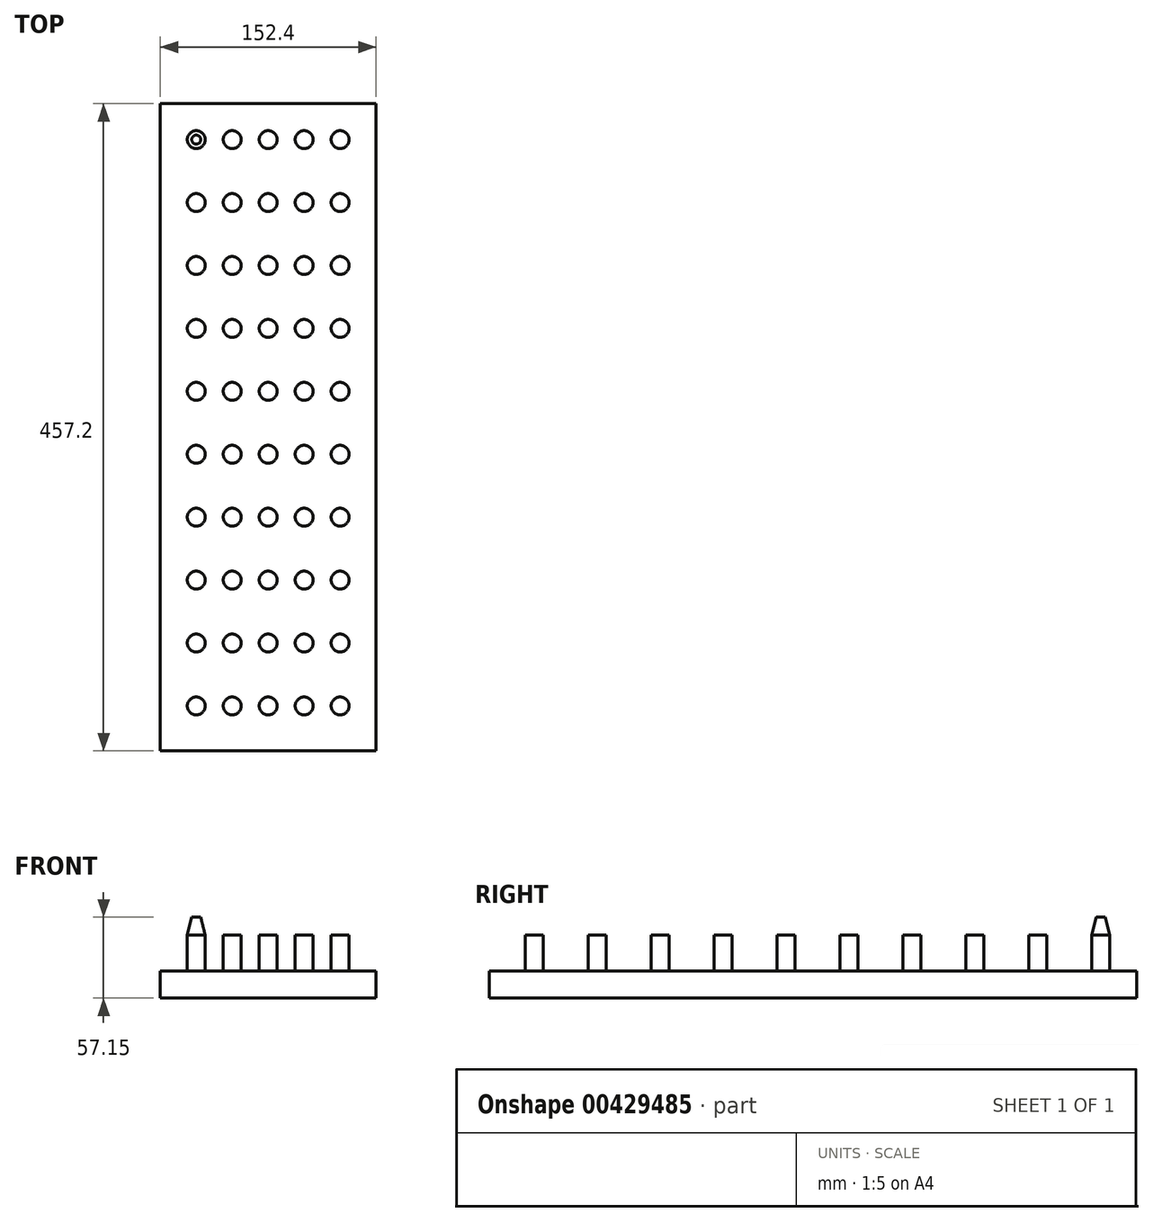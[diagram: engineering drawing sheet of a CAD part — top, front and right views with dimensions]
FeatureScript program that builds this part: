
annotation { "Feature Type Name" : "Feature", "Feature Type Description" : "" }
export const myFeature = defineFeature(function(context is Context, id is Id, definition is map)
    precondition{}
    {
        {
            var Q0;
            Q0=qCreatedBy(makeId("Front.planeOp"),FACE);
            var sketch = newSketch(context, id + "F0", { "sketchPlane" : qUnion([Q0])});
            skLineSegment(sketch, "E0.bottom", {"start": v(0, 0) * mm, "end": v(152.4, 0) * mm});
            skLineSegment(sketch, "E0.top", {"start": v(0, -19.05) * mm, "end": v(152.4, -19.05) * mm});
            skLineSegment(sketch, "E0.left", {"start": v(0, 0) * mm, "end": v(0, -19.05) * mm});
            skLineSegment(sketch, "E0.right", {"start": v(152.4, 0) * mm, "end": v(152.4, -19.05) * mm});
            skSolve(sketch);
        }
        {
            var Q0;
            Q0 = qSketchRegion(id + "F0", true);
            extrude(context, id + "F1", {"entities" : qUnion([Q0]), "depth" : 457.2 * mm});
        }
        {
            var Q0;
            Q0=makeQuery(id+"F1.opExtrude","SWEPT_FACE",FACE,{"disambiguationData":[OSD([sQuery(id+"F0.wireOp",EDGE,"E0.bottom")])]});
            var sketch = newSketch(context, id + "F2", { "sketchPlane" : qUnion([Q0])});
            skCircle(sketch, "E1", {"center": v(25.4, -25.4) * mm, "radius": 6.35 * mm});
            skCircle(sketch, "E2.0.1.0", {"center": v(25.4, -69.85) * mm, "radius": 6.35 * mm});
            skCircle(sketch, "E2.0.2.0", {"center": v(25.4, -114.3) * mm, "radius": 6.35 * mm});
            skCircle(sketch, "E2.0.3.0", {"center": v(25.4, -158.75) * mm, "radius": 6.35 * mm});
            skCircle(sketch, "E2.0.4.0", {"center": v(25.4, -203.2) * mm, "radius": 6.35 * mm});
            skCircle(sketch, "E2.0.5.0", {"center": v(25.4, -247.65) * mm, "radius": 6.35 * mm});
            skCircle(sketch, "E2.0.6.0", {"center": v(25.4, -292.1) * mm, "radius": 6.35 * mm});
            skCircle(sketch, "E2.0.7.0", {"center": v(25.4, -336.55) * mm, "radius": 6.35 * mm});
            skCircle(sketch, "E2.1.0.0", {"center": v(50.8, -25.4) * mm, "radius": 6.35 * mm});
            skCircle(sketch, "E2.1.1.0", {"center": v(50.8, -69.85) * mm, "radius": 6.35 * mm});
            skCircle(sketch, "E2.1.2.0", {"center": v(50.8, -114.3) * mm, "radius": 6.35 * mm});
            skCircle(sketch, "E2.1.3.0", {"center": v(50.8, -158.75) * mm, "radius": 6.35 * mm});
            skCircle(sketch, "E2.1.4.0", {"center": v(50.8, -203.2) * mm, "radius": 6.35 * mm});
            skCircle(sketch, "E2.1.5.0", {"center": v(50.8, -247.65) * mm, "radius": 6.35 * mm});
            skCircle(sketch, "E2.1.6.0", {"center": v(50.8, -292.1) * mm, "radius": 6.35 * mm});
            skCircle(sketch, "E2.1.7.0", {"center": v(50.8, -336.55) * mm, "radius": 6.35 * mm});
            skCircle(sketch, "E2.2.0.0", {"center": v(76.2, -25.4) * mm, "radius": 6.35 * mm});
            skCircle(sketch, "E2.2.1.0", {"center": v(76.2, -69.85) * mm, "radius": 6.35 * mm});
            skCircle(sketch, "E2.2.2.0", {"center": v(76.2, -114.3) * mm, "radius": 6.35 * mm});
            skCircle(sketch, "E2.2.3.0", {"center": v(76.2, -158.75) * mm, "radius": 6.35 * mm});
            skCircle(sketch, "E2.2.4.0", {"center": v(76.2, -203.2) * mm, "radius": 6.35 * mm});
            skCircle(sketch, "E2.2.5.0", {"center": v(76.2, -247.65) * mm, "radius": 6.35 * mm});
            skCircle(sketch, "E2.2.6.0", {"center": v(76.2, -292.1) * mm, "radius": 6.35 * mm});
            skCircle(sketch, "E2.2.7.0", {"center": v(76.2, -336.55) * mm, "radius": 6.35 * mm});
            skCircle(sketch, "E2.3.0.0", {"center": v(101.6, -25.4) * mm, "radius": 6.35 * mm});
            skCircle(sketch, "E2.3.1.0", {"center": v(101.6, -69.85) * mm, "radius": 6.35 * mm});
            skCircle(sketch, "E2.3.2.0", {"center": v(101.6, -114.3) * mm, "radius": 6.35 * mm});
            skCircle(sketch, "E2.3.3.0", {"center": v(101.6, -158.75) * mm, "radius": 6.35 * mm});
            skCircle(sketch, "E2.3.4.0", {"center": v(101.6, -203.2) * mm, "radius": 6.35 * mm});
            skCircle(sketch, "E2.3.5.0", {"center": v(101.6, -247.65) * mm, "radius": 6.35 * mm});
            skCircle(sketch, "E2.3.6.0", {"center": v(101.6, -292.1) * mm, "radius": 6.35 * mm});
            skCircle(sketch, "E2.3.7.0", {"center": v(101.6, -336.55) * mm, "radius": 6.35 * mm});
            skCircle(sketch, "E2.4.0.0", {"center": v(127, -25.4) * mm, "radius": 6.35 * mm});
            skCircle(sketch, "E2.4.1.0", {"center": v(127, -69.85) * mm, "radius": 6.35 * mm});
            skCircle(sketch, "E2.4.2.0", {"center": v(127, -114.3) * mm, "radius": 6.35 * mm});
            skCircle(sketch, "E2.4.3.0", {"center": v(127, -158.75) * mm, "radius": 6.35 * mm});
            skCircle(sketch, "E2.4.4.0", {"center": v(127, -203.2) * mm, "radius": 6.35 * mm});
            skCircle(sketch, "E2.4.5.0", {"center": v(127, -247.65) * mm, "radius": 6.35 * mm});
            skCircle(sketch, "E2.4.6.0", {"center": v(127, -292.1) * mm, "radius": 6.35 * mm});
            skCircle(sketch, "E2.4.7.0", {"center": v(127, -336.55) * mm, "radius": 6.35 * mm});
            skLineSegment(sketch, "E2.direction1", {"start": v(25.4, -25.4) * mm, "end": v(50.8, -25.4) * mm, "construction": true});
            skLineSegment(sketch, "E2.direction2", {"start": v(25.4, -25.4) * mm, "end": v(25.4, -69.85) * mm, "construction": true});
            skCircle(sketch, "E3.0.0.8", {"center": v(25.4, -381) * mm, "radius": 6.35 * mm});
            skCircle(sketch, "E3.0.0.9", {"center": v(25.4, -425.45) * mm, "radius": 6.35 * mm});
            skCircle(sketch, "E3.0.1.8", {"center": v(50.8, -381) * mm, "radius": 6.35 * mm});
            skCircle(sketch, "E3.0.1.9", {"center": v(50.8, -425.45) * mm, "radius": 6.35 * mm});
            skCircle(sketch, "E3.0.2.8", {"center": v(76.2, -381) * mm, "radius": 6.35 * mm});
            skCircle(sketch, "E3.0.2.9", {"center": v(76.2, -425.45) * mm, "radius": 6.35 * mm});
            skCircle(sketch, "E3.0.3.8", {"center": v(101.6, -381) * mm, "radius": 6.35 * mm});
            skCircle(sketch, "E3.0.3.9", {"center": v(101.6, -425.45) * mm, "radius": 6.35 * mm});
            skCircle(sketch, "E3.0.4.8", {"center": v(127, -381) * mm, "radius": 6.35 * mm});
            skCircle(sketch, "E3.0.4.9", {"center": v(127, -425.45) * mm, "radius": 6.35 * mm});
            skSolve(sketch);
        }
        {
            var Q0;
            Q0 = qSketchRegion(id + "F2", true);
            extrude(context, id + "F3", {"entities" : qUnion([Q0]), "operationType" : NewBodyOperationType.ADD, "depth" : 25.4 * mm});
        }
        {
            var Q0;
            Q0=makeQuery(id+"F3.opExtrude","CAP_FACE",FACE,{"disambiguationData":[OSD([sQuery(id+"F2.wireOp",EDGE,"E1")])],"isStart":false});
            var sketch = newSketch(context, id + "F4", { "sketchPlane" : qUnion([Q0])});
            skCircle(sketch, "E4.0", {"center": v(25.4, -25.4) * mm, "radius": 6.35 * mm});
            skCircle(sketch, "E4.1", {"center": v(50.8, -25.4) * mm, "radius": 6.35 * mm});
            skCircle(sketch, "E4.2", {"center": v(76.2, -25.4) * mm, "radius": 6.35 * mm});
            skCircle(sketch, "E4.3", {"center": v(101.6, -25.4) * mm, "radius": 6.35 * mm});
            skCircle(sketch, "E4.4", {"center": v(127, -25.4) * mm, "radius": 6.35 * mm});
            skSolve(sketch);
        }
        {
            var Q0;
            Q0=makeQuery(id+"F2.imprint","IMPRINT",FACE,{"disambiguationData":[TD([[makeQuery(id+"F2.imprint","IMPRINT",EDGE,{"derivedFrom":sQuery(id+"F2.wireOp",EDGE,"E1")}),-1.0]])]});
            cPlane(context, id + "F5", {"entities" : qUnion([Q0]), "cplaneType" : CPlaneType.OFFSET, "offset" : 38.1 * mm, "width" : 152.4 * mm, "height" : 152.4 * mm});
        }
        {
            var Q0;
            Q0=qCreatedBy(id+"F5.planeOp",FACE);
            var sketch = newSketch(context, id + "F6", { "sketchPlane" : qUnion([Q0])});
            skCircle(sketch, "E5", {"center": v(25.4, -25.4) * mm, "radius": 3.18 * mm});
            skCircle(sketch, "E6.1.0.0", {"center": v(50.8, -25.4) * mm, "radius": 3.18 * mm});
            skCircle(sketch, "E6.2.0.0", {"center": v(76.2, -25.4) * mm, "radius": 3.18 * mm});
            skCircle(sketch, "E6.3.0.0", {"center": v(101.6, -25.4) * mm, "radius": 3.18 * mm});
            skCircle(sketch, "E6.4.0.0", {"center": v(127, -25.4) * mm, "radius": 3.18 * mm});
            skLineSegment(sketch, "E6.direction1", {"start": v(25.4, -25.4) * mm, "end": v(50.8, -25.4) * mm, "construction": true});
            skSolve(sketch);
        }
        {
            var Q1;
            Q1=makeQuery(id+"F4.imprint","IMPRINT",FACE,{"disambiguationData":[TD([[makeQuery(id+"F4.imprint","IMPRINT",EDGE,{"derivedFrom":sQuery(id+"F4.wireOp",EDGE,"E4.0")}),1.0]])]});
            var Q2;
            Q2=makeQuery(id+"F6.imprint","IMPRINT",FACE,{"disambiguationData":[TD([[makeQuery(id+"F6.imprint","IMPRINT",EDGE,{"derivedFrom":sQuery(id+"F6.wireOp",EDGE,"E5")}),1.0]])]});
            loft(context, id + "F7", {"operationType" : NewBodyOperationType.ADD, "sheetProfilesArray" : [{ "sheetProfileEntities" : qUnion([Q1]) }, { "sheetProfileEntities" : qUnion([Q2]) }]});
        }
    });
